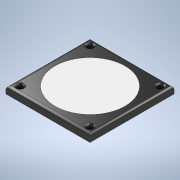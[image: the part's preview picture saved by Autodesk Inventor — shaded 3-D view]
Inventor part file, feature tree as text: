
AUTODESK INVENTOR PART (.ipt)
format: ipt  version: 2020 (Build 240168000, 168)  size: 148,480 bytes
history: native  units: mm
features: sketch x3, extrude x2, hole x1, fillet x1
ambient origin geometry x8: Origin, YZ Plane, XZ Plane, XY Plane, X Axis, Y Axis, Z Axis, Center Point
bodies: Solid1 (feature_tree)
feature tree (7):
  extrude  "Extrusion1"  Depth=60.0mm
  hole  "Hole1"  [1 undecoded]
  fillet  "Fillet1"  Radius=5.0mm
  extrude  "Extrusion2"  Depth=5.0mm
  sketch  "Sketch1"  dims[d0=60.0mm d1=60.0mm]
  sketch  "Sketch2"  dims[d2=5.0mm d3=0.0mm d4=5.0mm d6=5.0mm]
  sketch  "Sketch3"  dims[d7=5.0mm d8=5.0mm d9=5.0mm d10=5.0mm d11=5.0mm d12=5.0mm d13=4.3mm d14=6.0mm d15=6.0mm d16=2.0mm d17=90.0deg d18=8.0mm d19=20.594885mm d20=2.0mm d21=30.0mm d22=30.0mm d23=50.0mm d24=0.1mm d25=0.0mm]
note: 1 required parameter value undecoded (feature->parameter linkage not recoverable at this tier; creation-order binding heuristic only, values carry confidence <= 0.55)
